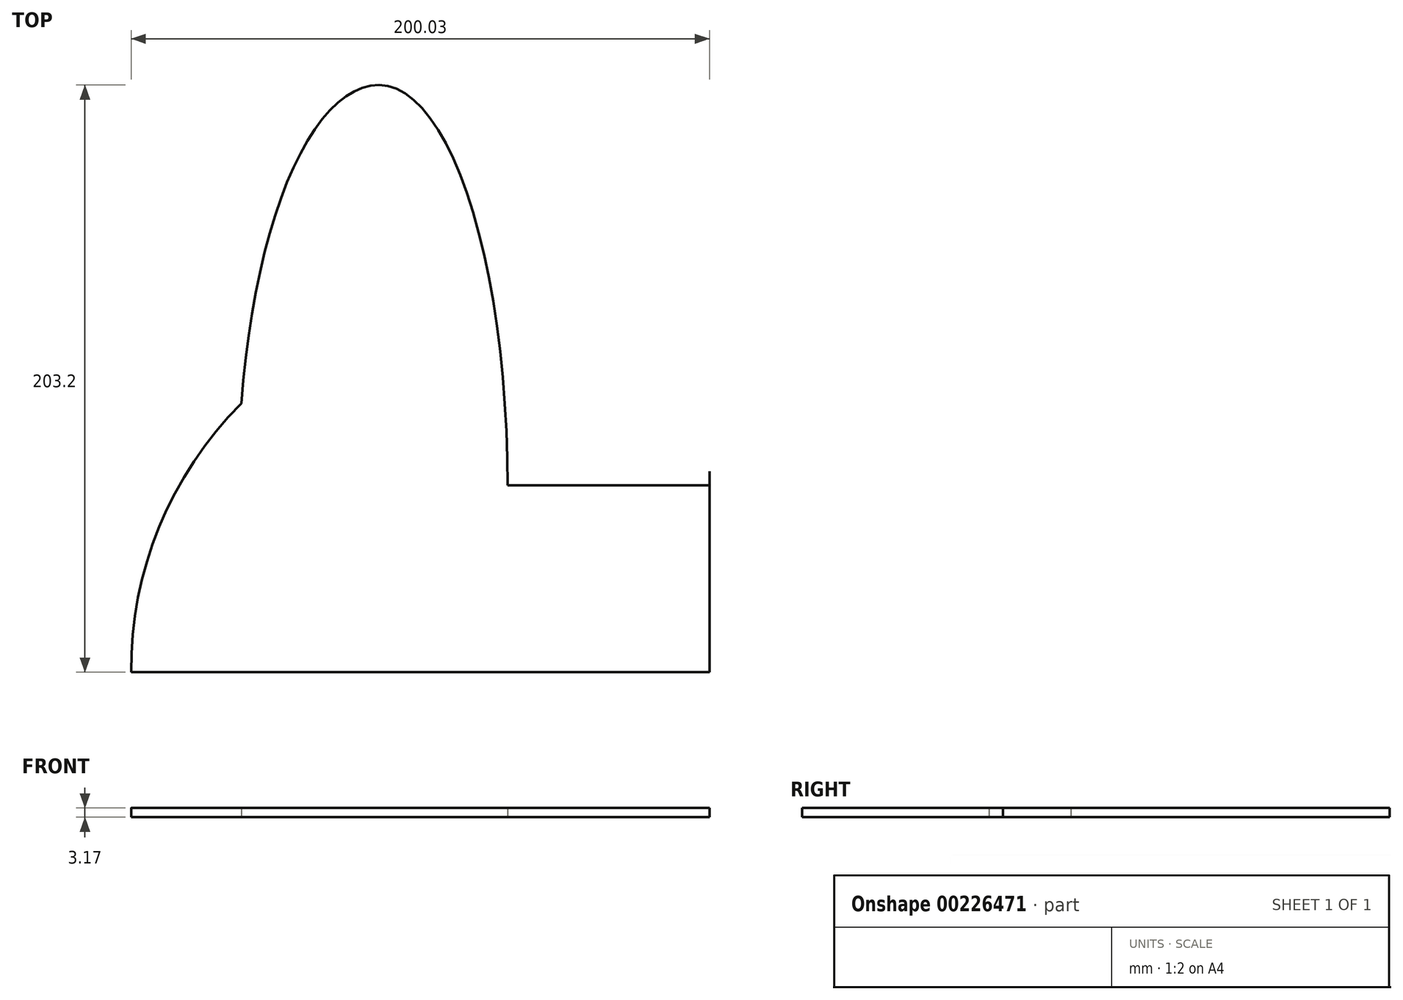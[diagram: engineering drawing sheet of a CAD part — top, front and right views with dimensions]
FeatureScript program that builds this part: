
annotation { "Feature Type Name" : "Feature", "Feature Type Description" : "" }
export const myFeature = defineFeature(function(context is Context, id is Id, definition is map)
    precondition{}
    {
        {
            var Q0;
            Q0=qCreatedBy(makeId("Top.planeOp"),FACE);
            var sketch = newSketch(context, id + "F0", { "sketchPlane" : qUnion([Q0])});
            skFitSpline(sketch, "E0.0", {"points": [v(69.8, 58.12) * mm, v(69.84, 68.36) * mm, v(70.22, 87.98) * mm, v(71.69, 114.79) * mm, v(75.52, 145.39) * mm, v(83.67, 175.1) * mm, v(95.26, 195.67) * mm, v(109.84, 205.98) * mm, v(125.92, 203.24) * mm, v(140.85, 184.98) * mm, v(152.9, 155.87) * mm, v(159.11, 128.89) * mm, v(161.46, 109.34) * mm, v(161.95, 97) * mm, v(161.93, 91.01) * mm]});
            skArc(sketch, "E0.1", {"start": v(161.93, 92.98) * mm, "mid": v(190.31, 50.32) * mm, "end": v(200.03, 0) * mm});
            skLineSegment(sketch, "E0.2", {"start": v(200.03, 0) * mm, "end": v(69.85, 0) * mm});
            skLineSegment(sketch, "E1", {"start": v(-100.7, 203.2) * mm, "end": v(133.94, 203.2) * mm, "construction": true});
            skPoint(sketch, "E2", {"position": v(114.3, 203.2) * mm});
            skLineSegment(sketch, "E3", {"start": v(69.85, 64.65) * mm, "end": v(69.85, 0) * mm});
            skLineSegment(sketch, "E4", {"start": v(114.3, 203.2) * mm, "end": v(114.3, 0) * mm, "construction": true});
            skEllipticalArc(sketch, "E5", {});
            skLineSegment(sketch, "E6", {"start": v(69.85, 64.65) * mm, "end": v(69.85, 227.16) * mm, "construction": true});
            skLineSegment(sketch, "E7", {"start": v(69.93, 1) * mm, "end": v(161.93, 92.98) * mm, "construction": true});
            skLineSegment(sketch, "E8.MirrorCS", {"start": v(0, 64.65) * mm, "end": v(0, 0) * mm});
            skLineSegment(sketch, "E9.MirrorCS", {"start": v(0, 64.65) * mm, "end": v(0, 307.16) * mm, "construction": true});
            skLineSegment(sketch, "E10.MirrorCS", {"start": v(-0.08, 1) * mm, "end": v(-92.08, 92.99) * mm, "construction": true});
            skArc(sketch, "E11.MirrorCS", {"start": v(-92.08, 92.99) * mm, "mid": v(-120.47, 50.32) * mm, "end": v(-130.17, 0) * mm});
            skLineSegment(sketch, "E12.MirrorCS", {"start": v(-44.45, 203.2) * mm, "end": v(-44.45, 0) * mm, "construction": true});
            skLineSegment(sketch, "E13.MirrorCS", {"start": v(-130.18, 0) * mm, "end": v(0, 0) * mm});
            skPoint(sketch, "E14.MirrorP", {"position": v(-44.45, 203.2) * mm});
            skPoint(sketch, "E15.center.orphan", {"position": v(-44.45, 64.65) * mm});
            skEllipticalArc(sketch, "E16", {});
            skLineSegment(sketch, "E17.bottom", {"start": v(0, 64.65) * mm, "end": v(69.85, 64.65) * mm});
            skLineSegment(sketch, "E17.top", {"start": v(0, 0) * mm, "end": v(69.85, 0) * mm});
            skEllipticalArc(sketch, "E18", {});
            skLineSegment(sketch, "E19", {"start": v(34.93, 64.65) * mm, "end": v(34.93, -21.77) * mm, "construction": true});
            skLineSegment(sketch, "E20.top", {"start": v(0, 450.73) * mm, "end": v(69.85, 450.73) * mm});
            skLineSegment(sketch, "E20.left", {"start": v(0, 64.65) * mm, "end": v(0, 450.73) * mm});
            skLineSegment(sketch, "E20.right", {"start": v(69.85, 64.65) * mm, "end": v(69.85, 450.73) * mm});
            skLineSegment(sketch, "E21.bottom", {"start": v(47.63, 331.35) * mm, "end": v(22.23, 331.35) * mm});
            skLineSegment(sketch, "E21.top", {"start": v(47.63, 344.05) * mm, "end": v(22.23, 344.05) * mm});
            skLineSegment(sketch, "E21.left", {"start": v(47.63, 331.35) * mm, "end": v(47.63, 344.05) * mm});
            skLineSegment(sketch, "E21.right", {"start": v(22.23, 331.35) * mm, "end": v(22.23, 344.05) * mm});
            skPoint(sketch, "E21.middle", {"position": v(34.93, 337.7) * mm});
            const initialGuessF0  = {"E5": [0.1143, 0.0646534590532031, 0, 1, 0.1385465409467969, 0.04445, 0, 1.5707963267948966], "E16": [-0.04445, 0.0646534590532031, 0, 1, 0.13854654094679691, 0.04445, 4.71238898038469, 0], "E18": [-0.04445, 0.0646534590532031, 0, 1, 0.13854654094679691, 0.04865344734233295, 0, 1.3648200427235055]};
            skSetInitialGuess(sketch, initialGuessF0);
            skSolve(sketch);
        }
        {
            var Q0;
            Q0=makeQuery(id+"F0.imprint","IMPRINT",FACE,{"disambiguationData":[TD([[makeQuery(id+"F0.imprint","IMPRINT",EDGE,{"derivedFrom":sQuery(id+"F0.wireOp",EDGE,"E17.bottom")}),1.0]])]});
            var Q1;
            Q1=makeQuery(id+"F0.imprint","IMPRINT",FACE,{"disambiguationData":[TD([[makeQuery(id+"F0.imprint","IMPRINT",EDGE,{"derivedFrom":sQuery(id+"F0.wireOp",EDGE,"E11.MirrorCS")}),1.0]])]});
            var Q2;
            Q2=makeQuery(id+"F0.imprint","IMPRINT",FACE,{"disambiguationData":[TD([[makeQuery(id+"F0.imprint","IMPRINT",EDGE,{"derivedFrom":sQuery(id+"F0.wireOp",EDGE,"E17.top")}),1.0]])]});
            var Q3;
            Q3=makeQuery(id+"F0.imprint","IMPRINT",FACE,{"disambiguationData":[TD([[makeQuery(id+"F0.imprint","IMPRINT",EDGE,{"derivedFrom":sQuery(id+"F0.wireOp",EDGE,"E0.0")}),-1.0]])]});
            extrude(context, id + "F1", {"entities" : qUnion([Q0, Q1, Q2, Q3]), "depth" : 3.17 * mm});
        }
    });
